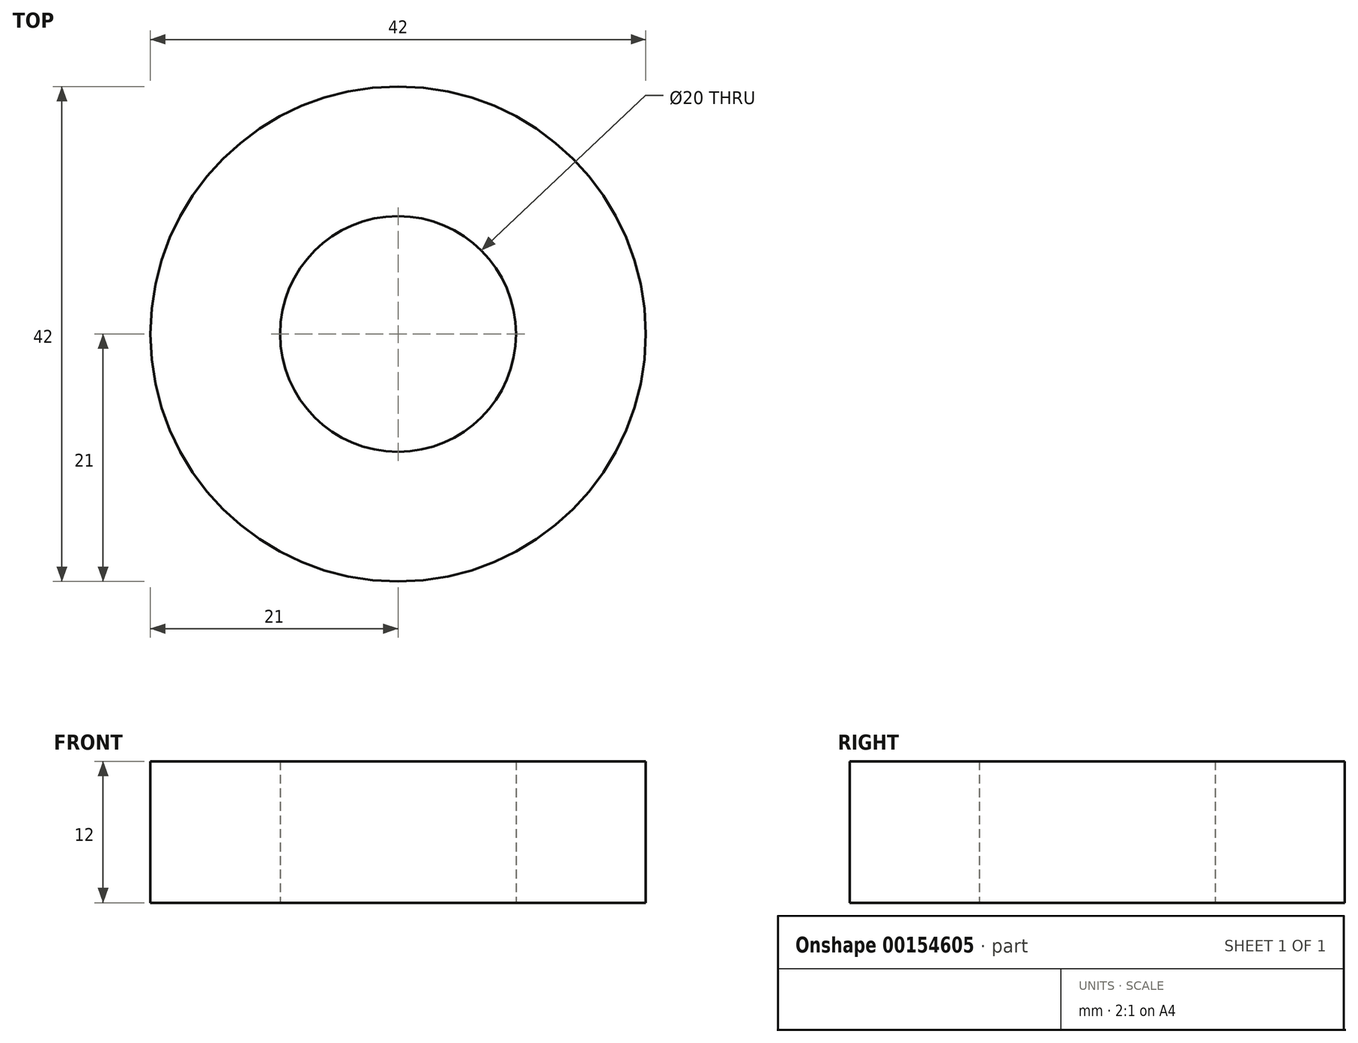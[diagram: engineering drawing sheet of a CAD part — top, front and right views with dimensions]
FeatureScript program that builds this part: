
annotation { "Feature Type Name" : "Feature", "Feature Type Description" : "" }
export const myFeature = defineFeature(function(context is Context, id is Id, definition is map)
    precondition{}
    {
        {
            var Q0;
            Q0=qCreatedBy(makeId("Top.planeOp"),FACE);
            var sketch = newSketch(context, id + "F1", { "sketchPlane" : qUnion([Q0])});
            skCircle(sketch, "E0", {"center": v(0, 0) * mm, "radius": 10 * mm});
            skCircle(sketch, "E1", {"center": v(0, 0) * mm, "radius": 21 * mm});
            skSolve(sketch);
        }
        {
            var Q0;
            Q0=makeQuery(id+"F1.imprint","IMPRINT",FACE,{"disambiguationData":[TD([[makeQuery(id+"F1.imprint","IMPRINT",EDGE,{"derivedFrom":sQuery(id+"F1.wireOp",EDGE,"E0")}),-1.0]])]});
            extrude(context, id + "F0", {"entities" : qUnion([Q0]), "depth" : 12 * mm, "symmetric" : true});
        }
    });
